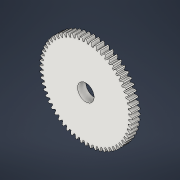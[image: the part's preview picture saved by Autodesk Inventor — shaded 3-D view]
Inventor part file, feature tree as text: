
AUTODESK INVENTOR PART (.ipt)
format: ipt  version: 2021 (Build 250183000, 183)  size: 393,216 bytes
history: native  units: mm (DEFAULTED — no unit token found)
features: plane x3, other x3, sketch x3, extrude x2
ambient origin geometry x8: Origin, YZ Plane, XZ Plane, XY Plane, X Axis, Y Axis, Z Axis, Center Point
bodies: Solid1 (feature_tree)
feature tree (11):
  extrude  "Extrusion1"  Depth=0.5mm TaperAngle=0.0deg
  plane  "Work Plane2"
  plane  "Work Plane8"
  plane  "Work Plane9"
  other  "Engrenagem reta"
  extrude  "Extrusão2"  Depth=10.0mm TaperAngle=0.0deg
  sketch  "Sketch1"  dims[d0=5.575177mm d1=0.5mm d2=0.0mm]
  sketch  "Sketch2"  dims[d3=5.4mm d4=10.0mm d5=0.0mm]
  other  "Srf1"
  sketch  "Esboço3"  dims[d16=3.597588mm d17=0.0mm d34=0.523599mm d39=0.0mm d41=0.0mm d43=3.597588mm d46=3.597588mm d47=0.0mm d48=0.0mm d49=1.0mm d50=0.5mm d51=0.0mm]
  other  "Diâmetro do flanco"
